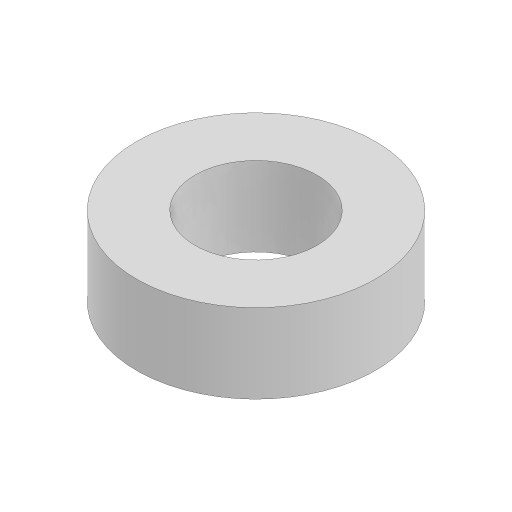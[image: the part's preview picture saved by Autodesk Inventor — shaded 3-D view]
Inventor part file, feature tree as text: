
AUTODESK INVENTOR PART (.ipt)
format: ipt  version: 2024 (Build 280153000, 153)  size: 98,816 bytes
history: native  units: mm
features: extrude x1, direct_edit x1, sketch x1, other x1
ambient origin geometry x8: Origin, YZ Plane, XZ Plane, XY Plane, X Axis, Y Axis, Z Axis, Center Point
bodies: Solid1 (feature_tree)
feature tree (4):
  extrude  "Extrusion1"  Depth=6.35mm
  direct_edit  "Direct Edit1"
  sketch  "Sketch1"  dims[d0=9.525mm d1=4.8mm d2=6.35mm d3=0.0mm d4=-0.127mm]
  other  "Size1"
